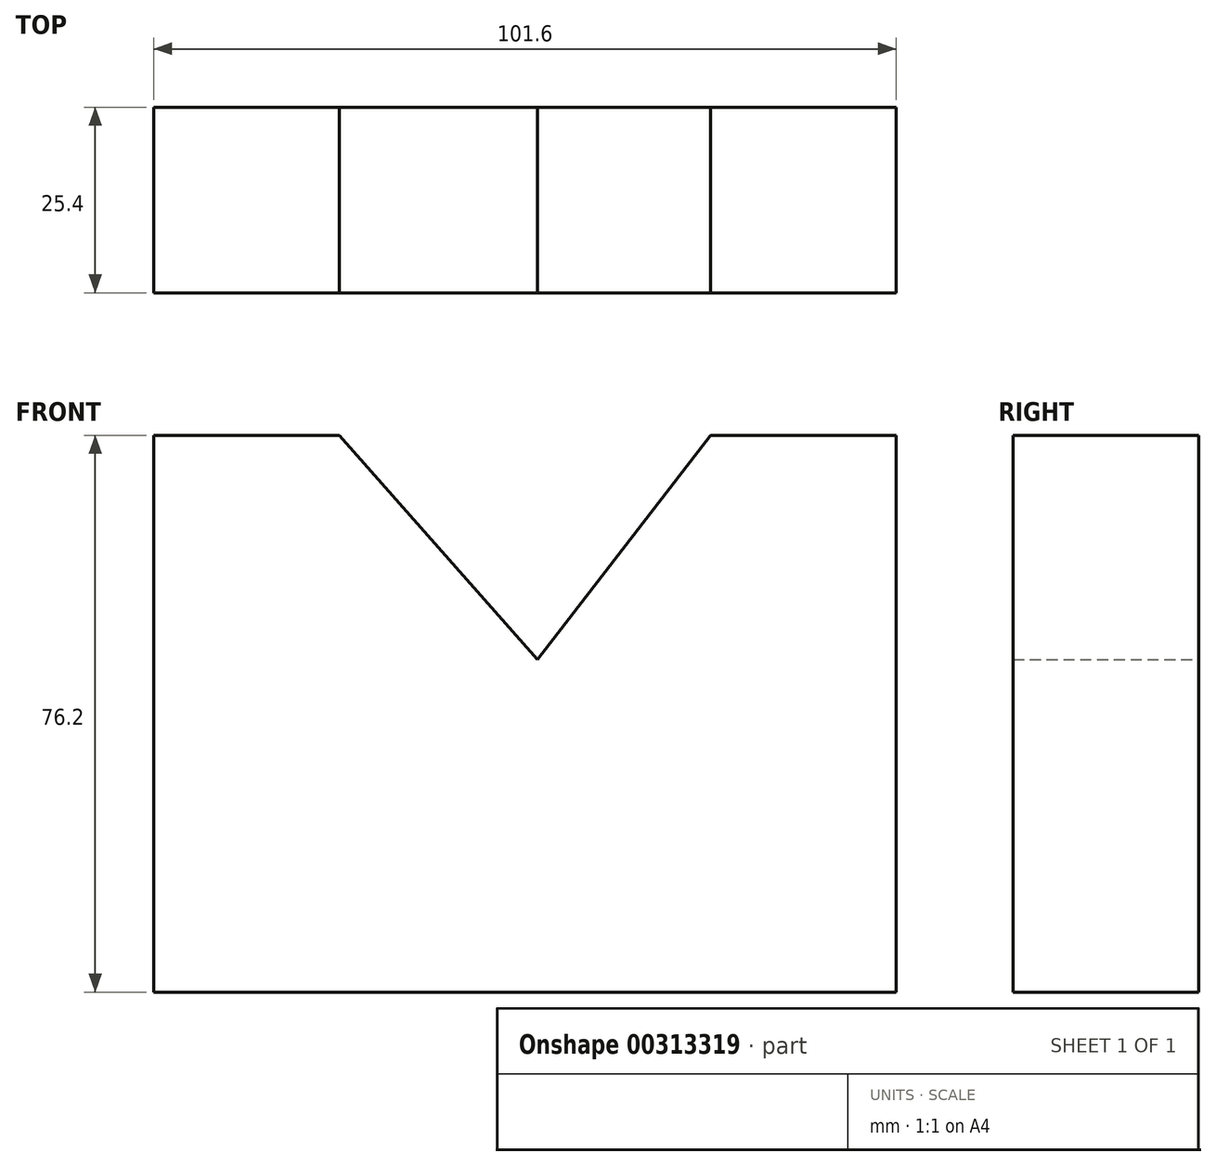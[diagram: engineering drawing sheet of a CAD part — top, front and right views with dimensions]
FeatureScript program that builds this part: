
annotation { "Feature Type Name" : "Feature", "Feature Type Description" : "" }
export const myFeature = defineFeature(function(context is Context, id is Id, definition is map)
    precondition{}
    {
        {
            var Q0;
            Q0=qCreatedBy(makeId("Front.planeOp"),FACE);
            var sketch = newSketch(context, id + "F0", { "sketchPlane" : qUnion([Q0])});
            skLineSegment(sketch, "E0", {"start": v(-52.51, -45.5) * mm, "end": v(49.09, -45.5) * mm});
            skLineSegment(sketch, "E1", {"start": v(-52.51, -45.5) * mm, "end": v(-52.51, 30.7) * mm});
            skLineSegment(sketch, "E2", {"start": v(49.09, -45.5) * mm, "end": v(49.09, 30.7) * mm});
            skLineSegment(sketch, "E3", {"start": v(49.09, 30.7) * mm, "end": v(23.69, 30.7) * mm});
            skLineSegment(sketch, "E4", {"start": v(-52.51, 30.7) * mm, "end": v(-27.11, 30.7) * mm});
            skLineSegment(sketch, "E5", {"start": v(-27.11, 30.7) * mm, "end": v(0, 0) * mm});
            skLineSegment(sketch, "E6", {"start": v(0, 0) * mm, "end": v(23.69, 30.7) * mm});
            skSolve(sketch);
        }
        {
            var Q0;
            Q0=makeQuery(id+"F0.imprint","IMPRINT",FACE,{"disambiguationData":[TD([[makeQuery(id+"F0.imprint","IMPRINT",EDGE,{"derivedFrom":sQuery(id+"F0.wireOp",EDGE,"E0")}),1.0]])]});
            extrude(context, id + "F1", {"entities" : qUnion([Q0]), "depth" : 25.4 * mm});
        }
    });
